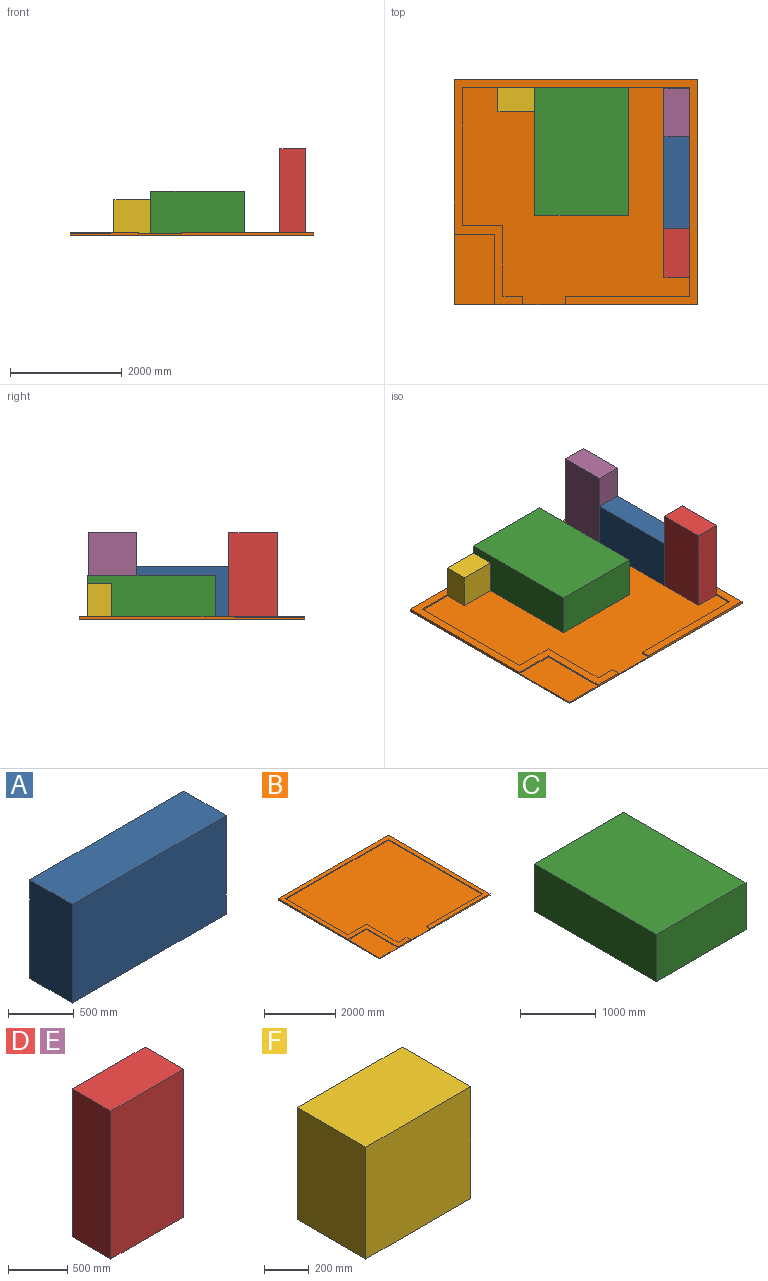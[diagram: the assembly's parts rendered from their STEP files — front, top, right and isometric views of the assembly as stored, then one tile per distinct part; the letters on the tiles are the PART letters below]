
ASSEMBLY  parts=6 mates=13
PART A: 6 faces, bbox 1651x457.2x914.4 mm
  f0: plane 914.4x457.2mm, normal (1,0,0), area 418063.7mm2, adj f1,f3,f4,f5
  f1: plane 1651x914.4mm, normal (0,1,0), area 1509674.4mm2, adj f0,f2,f4,f5
  f2: plane 914.4x457.2mm, normal (-1,0,0), area 418063.7mm2, adj f1,f3,f4,f5
  f3: plane 1651x914.4mm, normal (0,-1,0), area 1509674.4mm2, adj f0,f2,f4,f5
  f4: plane 1651x457.2mm, normal (0,0,1), area 754837.2mm2, adj f0,f1,f2,f3
  f5: plane 1651x457.2mm, normal (0,0,-1), area 754837.2mm2, adj f0,f1,f2,f3
PART B: 19 faces, bbox 4368.8x4038.6x50.8 mm
  f0: plane 4368.8x50.8mm, normal (0,-1,0), area 184193.2mm2, adj f1,f9,f10,f12,f14,f15,f16,f17
  f1: plane 152.4x25.4mm, normal (1,0,0), area 3871mm2, adj f0,f2,f15,f18
  f2: plane 355.6x25.4mm, normal (0,1,0), area 9032.2mm2, adj f1,f3,f15,f18
  f3: plane 1263.65x25.4mm, normal (1,0,0), area 32096.7mm2, adj f2,f4,f15,f18
  f4: plane 723.9x25.4mm, normal (0,1,0), area 18387.1mm2, adj f3,f5,f15,f18
  f5: plane 2470.15x25.4mm, normal (1,0,0), area 62741.8mm2, adj f4,f6,f15,f18
  f6: plane 4064x25.4mm, normal (0,-1,0), area 103225.6mm2, adj f5,f7,f15,f18
  f7: plane 3733.8x25.4mm, normal (-1,0,0), area 94838.5mm2, adj f6,f8,f15,f18
  f8: plane 2222.5x25.4mm, normal (0,1,0), area 56451.5mm2, adj f7,f9,f15,f18
  f9: plane 152.4x25.4mm, normal (-1,0,0), area 3871mm2, adj f0,f8,f15,f18
  f10: plane 4038.6x50.8mm, normal (1,0,0), area 205160.9mm2, adj f0,f11,f15,f16
  f11: plane 4368.8x50.8mm, normal (0,1,0), area 221935mm2, adj f10,f12,f15,f16
  f12: plane 4038.6x50.8mm, normal (-1,0,0), area 173064.2mm2, adj f0,f11,f13,f15,f16,f17
  f13: plane 723.9x25.4mm, normal (0,-1,0), area 18387.1mm2, adj f12,f14,f15,f17
  f14: plane 1263.65x25.4mm, normal (-1,0,0), area 32096.7mm2, adj f0,f13,f15,f17
  f15: plane 4368.8x4038.6mm, normal (0,0,1), area 2353543.7mm2, adj f0,f1,f2,f3,f4,f5,f6,f7
  f16: plane 4368.8x4038.6mm, normal (0,0,-1), area 17643835.7mm2, adj f0,f10,f11,f12
  f17: plane 1263.65x723.9mm, normal (0,0,1), area 914756.2mm2, adj f0,f12,f13,f14
  f18: plane 4064x3886.2mm, normal (0,0,1), area 14375535.8mm2, adj f0,f1,f2,f3,f4,f5,f6,f7
PART C: 6 faces, bbox 1676.4x2286x762 mm
  f0: plane 2286x762mm, normal (1,0,0), area 1741932mm2, adj f1,f3,f4,f5
  f1: plane 1676.4x762mm, normal (0,1,0), area 1277416.8mm2, adj f0,f2,f4,f5
  f2: plane 2286x762mm, normal (-1,0,0), area 1741932mm2, adj f1,f3,f4,f5
  f3: plane 1676.4x762mm, normal (0,-1,0), area 1277416.8mm2, adj f0,f2,f4,f5
  f4: plane 2286x1676.4mm, normal (0,0,1), area 3832250.4mm2, adj f0,f1,f2,f3
  f5: plane 2286x1676.4mm, normal (0,0,-1), area 3832250.4mm2, adj f0,f1,f2,f3
PART D: 6 faces, bbox 863.6x457.2x1524 mm
  f0: plane 1524x863.6mm, normal (0,1,0), area 1316126.4mm2, adj f1,f3,f4,f5
  f1: plane 1524x457.2mm, normal (-1,0,0), area 696772.8mm2, adj f0,f2,f4,f5
  f2: plane 1524x863.6mm, normal (0,-1,0), area 1316126.4mm2, adj f1,f3,f4,f5
  f3: plane 1524x457.2mm, normal (1,0,0), area 696772.8mm2, adj f0,f2,f4,f5
  f4: plane 863.6x457.2mm, normal (0,0,1), area 394837.9mm2, adj f0,f1,f2,f3
  f5: plane 863.6x457.2mm, normal (0,0,-1), area 394837.9mm2, adj f0,f1,f2,f3
PART E: same geometry as D
PART F: 6 faces, bbox 660.4x431.8x609.6 mm
  f0: plane 660.4x609.6mm, normal (0,1,0), area 402579.8mm2, adj f1,f3,f4,f5
  f1: plane 609.6x431.8mm, normal (-1,0,0), area 263225.3mm2, adj f0,f2,f4,f5
  f2: plane 660.4x609.6mm, normal (0,-1,0), area 402579.8mm2, adj f1,f3,f4,f5
  f3: plane 609.6x431.8mm, normal (1,0,0), area 263225.3mm2, adj f0,f2,f4,f5
  f4: plane 660.4x431.8mm, normal (0,0,1), area 285160.7mm2, adj f0,f1,f2,f3
  f5: plane 660.4x431.8mm, normal (0,0,-1), area 285160.7mm2, adj f0,f1,f2,f3
PLACE A rot(axis=(0,0,1),90deg) t=(1518.77,201.9,303.63)mm
PLACE B t=(-590.73,569.45,278.23)mm fixed
PLACE C t=(-183.52,761.99,303.63)mm
PLACE D rot(axis=(0,0,1),90deg) t=(1518.77,-1055.4,303.63)mm
PLACE E rot(axis=(0,0,1),90deg) t=(1518.77,1459.2,303.63)mm
PLACE F t=(-1351.92,1689.09,303.63)mm
MATE planar F.f3 <-> C.f2  axis (1,0,0) through (-1021.72,1689.09,608.43)mm
MATE planar A.f5 <-> B.f18  axis (0,0,-1) through (1518.77,201.9,303.63)mm
MATE planar F.f5 <-> B.f18  axis (0,0,-1) through (-1351.92,1689.09,303.63)mm
MATE planar A.f3 <-> B.f7  axis (1,0,0) through (1747.37,201.9,760.83)mm
MATE planar C.f1 <-> B.f6  axis (0,1,0) through (-183.52,1904.99,684.63)mm
MATE planar F.f0 <-> C.f1  axis (0,1,0) through (-1351.92,1904.99,608.43)mm
MATE planar C.f5 <-> B.f18  axis (0,0,-1) through (-183.52,761.99,303.63)mm
MATE planar D.f0 <-> A.f1  axis (-1,0,0) through (1290.17,-1055.4,1065.63)mm
MATE planar E.f5 <-> B.f18  axis (0,0,-1) through (1518.77,1459.2,303.63)mm
MATE planar A.f0 <-> E.f1  axis (0,1,0) through (1518.77,1027.4,760.83)mm
MATE planar D.f5 <-> B.f18  axis (0,0,-1) through (1518.77,-1055.4,303.63)mm
MATE planar E.f0 <-> A.f1  axis (-1,0,0) through (1290.17,1459.2,1065.63)mm
MATE planar A.f2 <-> D.f3  axis (0,-1,0) through (1518.77,-623.6,760.83)mm
